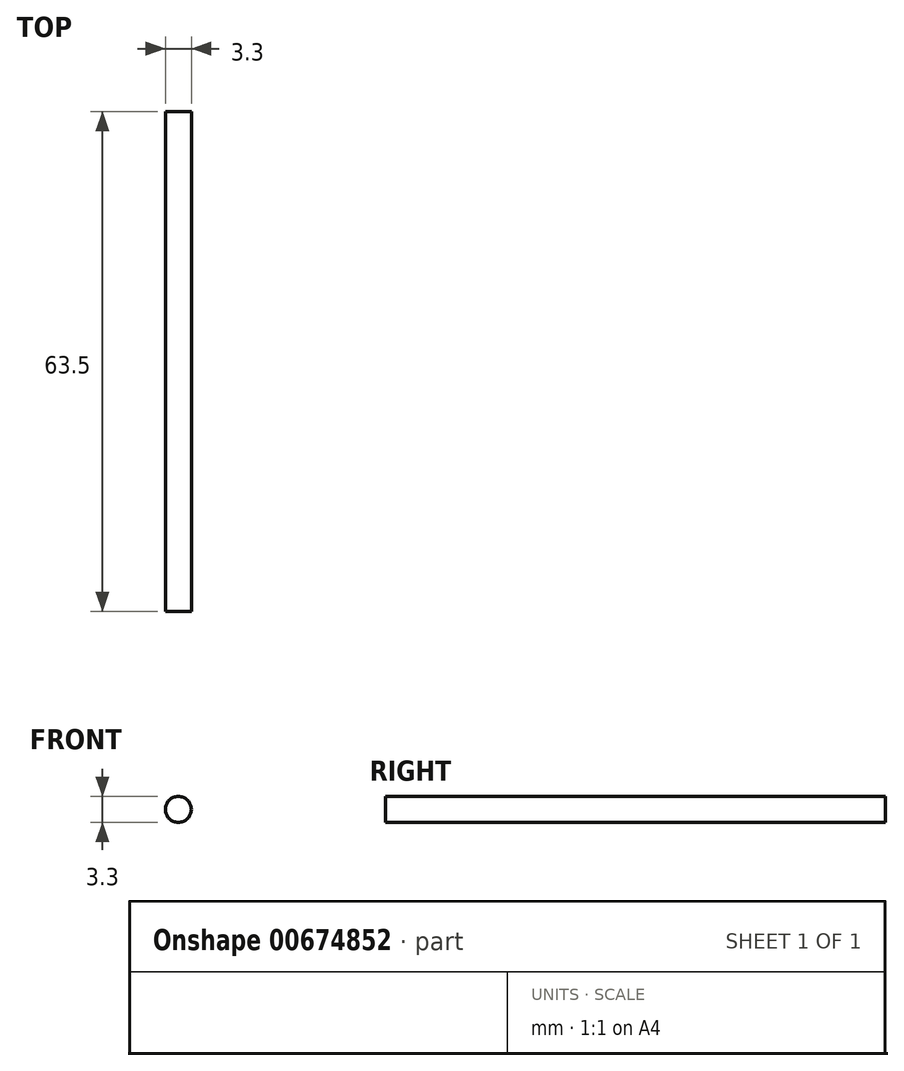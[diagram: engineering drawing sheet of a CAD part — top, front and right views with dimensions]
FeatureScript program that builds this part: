
annotation { "Feature Type Name" : "Feature", "Feature Type Description" : "" }
export const myFeature = defineFeature(function(context is Context, id is Id, definition is map)
    precondition{}
    {
        {
            var Q0;
            Q0=qCreatedBy(makeId("Front.planeOp"),FACE);
            var sketch = newSketch(context, id + "F0", { "sketchPlane" : qUnion([Q0])});
            skCircle(sketch, "E0", {"center": v(0, 0) * mm, "radius": 1.65 * mm});
            skSolve(sketch);
        }
        {
            var Q0;
            Q0=makeQuery(id+"F0.imprint","IMPRINT",FACE,{"disambiguationData":[TD([[makeQuery(id+"F0.imprint","IMPRINT",EDGE,{"derivedFrom":sQuery(id+"F0.wireOp",EDGE,"E0")}),1.0]])]});
            extrude(context, id + "F1", {"entities" : qUnion([Q0]), "oppositeDirection" : true, "depth" : 63.5 * mm, "offsetDistance" : 25.4 * mm});
        }
    });
